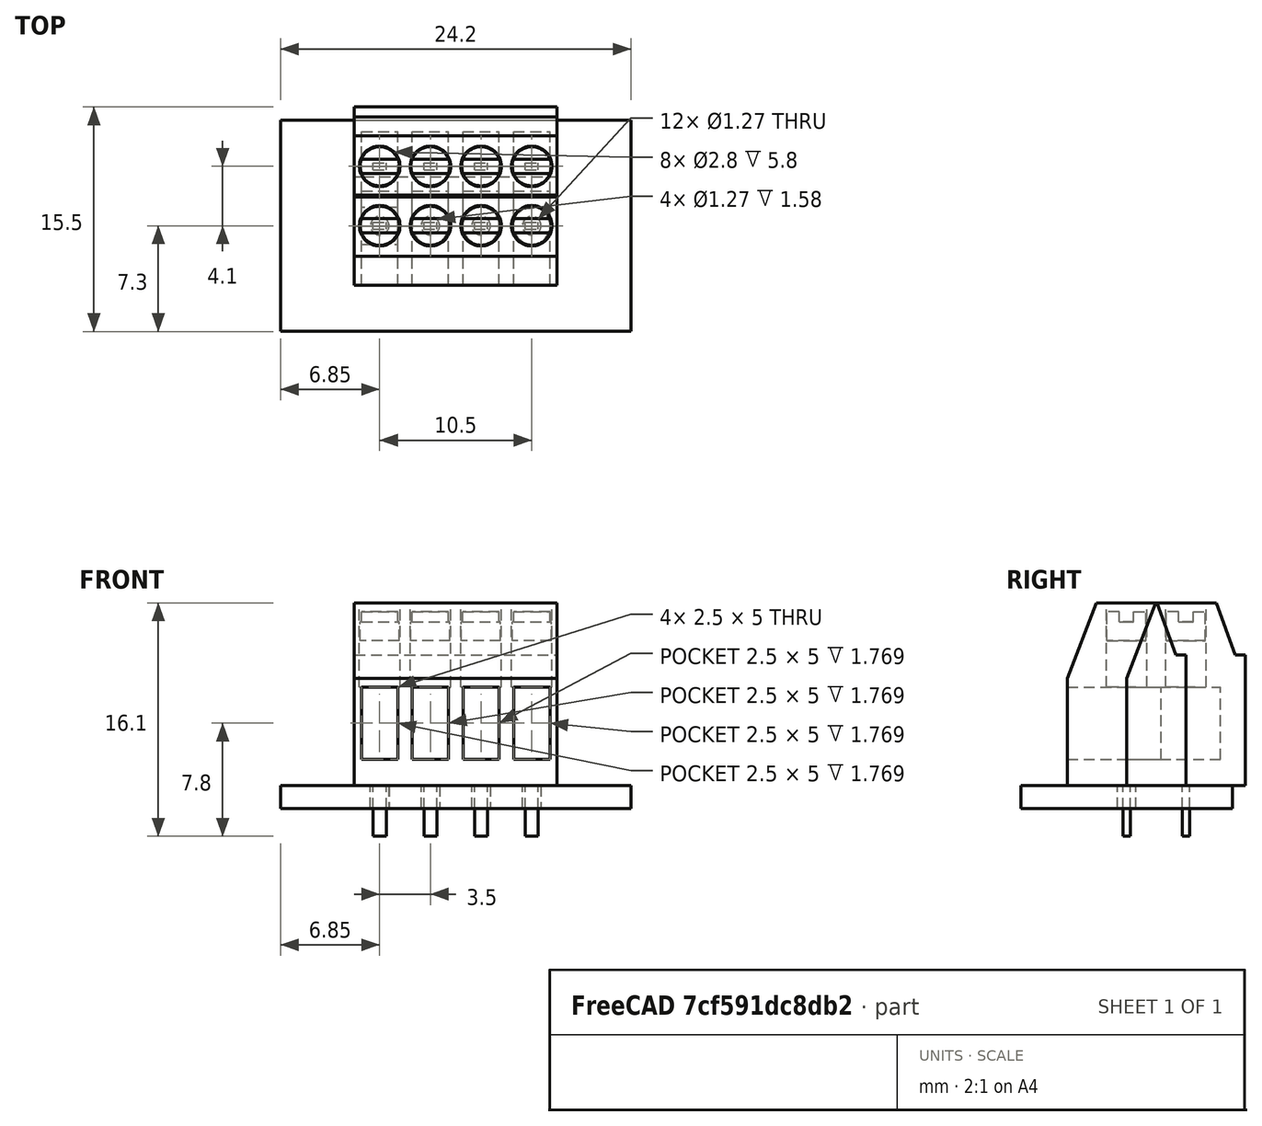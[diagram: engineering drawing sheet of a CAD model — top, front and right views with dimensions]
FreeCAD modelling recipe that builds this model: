
FCSTD DOCUMENT  (FreeCAD 0.18R16131 (Git))
Label: TerminalBlock_TE_284391-4_Angled_1x04_P3.50mm
License: All rights reserved
LicenseURL: http://en.wikipedia.org/wiki/All_rights_reserved
objects: Part::Box×12, Part::Cut×12, Part::Cylinder×8, Part::FeaturePython×6, App::DocumentObjectGroup×2, Part::Part2DObjectPython×1, Part::Extrusion×1, App::Part×1, Part::Feature×1
note: 41 computed .brp shape members not serialized (recipe doc carries the construction recipe); baked Part::Feature solids carry a one-line shape summary decoded from their .brp

FEATURE [Part::Part2DObjectPython] Wire  # Draft 2D object (typed FeaturePython)
  ChamferSize = 0
  Closed = true
  End = (0,0,0)
  FilletRadius = 0
  Length = 38.8989
  MakeFace = true
  Placement = pos=(0,0,0) rot=(0.57735,0.57735,0.57735;2.0944rad)
  Points = (8) [(0,0,0),(0,7.4,0),(2,12.6,0),(6.2,12.6,0),(7.5,9,0),(8.2,9,0),(8.2,0,0),(0,0,0)]
  Start = (0,0,0)
  Subdivisions = 0
FEATURE [Part::Extrusion] Extrude
  Base = -> Wire
  Dir = (1,0,0)
  DirMode = 2
  FaceMakerClass = Part::FaceMakerBullseye
  LengthFwd = 14
  LengthRev = 0
  Solid = false
  Symmetric = true
FEATURE [Part::Box] Box  label="Pin 1"
  AttacherType = Attacher::AttachEngine3D
  Height = 3.5
  Length = 0.9
  Placement = pos=(-5.7,3.85,-3.5) rot=(0,0,1;0rad)
  Width = 0.5
FEATURE [Part::Box] Box001  label="Pin 2"
  AttacherType = Attacher::AttachEngine3D
  Height = 3.5
  Length = 0.9
  Placement = pos=(-2.2,3.85,-3.5) rot=(0,0,1;0rad)
  Width = 0.5
FEATURE [Part::Box] Box002  label="Pin 3"
  AttacherType = Attacher::AttachEngine3D
  Height = 3.5
  Length = 0.9
  Placement = pos=(1.3,3.85,-3.5) rot=(0,0,1;0rad)
  Width = 0.5
FEATURE [Part::Box] Box003  label="Pin 4"
  AttacherType = Attacher::AttachEngine3D
  Height = 3.5
  Length = 0.9
  Placement = pos=(4.8,3.85,-3.5) rot=(0,0,1;0rad)
  Width = 0.5
FEATURE [App::DocumentObjectGroup] Group  label="Pins"
  Group = -> [Box,Box001,Box002,Box003]
FEATURE [Part::Cylinder] Cylinder
  Angle = 360
  AttacherType = Attacher::AttachEngine3D
  Height = 6.1
  Placement = pos=(1.75,4.1,6.8) rot=(0,0,1;0rad)
  Radius = 1.4
FEATURE [Part::Cylinder] Cylinder001
  Angle = 360
  AttacherType = Attacher::AttachEngine3D
  Height = 6.1
  Placement = pos=(5.25,4.1,6.8) rot=(0,0,1;0rad)
  Radius = 1.4
FEATURE [Part::Cylinder] Cylinder002
  Angle = 360
  AttacherType = Attacher::AttachEngine3D
  Height = 6.1
  Placement = pos=(-1.75,4.1,6.8) rot=(0,0,1;0rad)
  Radius = 1.4
FEATURE [Part::Cylinder] Cylinder003
  Angle = 360
  AttacherType = Attacher::AttachEngine3D
  Height = 6.1
  Placement = pos=(-5.25,4.1,6.8) rot=(0,0,1;0rad)
  Radius = 1.4
FEATURE [Part::Cut] Cut
  Base = -> Extrude
  Tool = -> Cylinder
FEATURE [Part::Cut] Cut001
  Base = -> Cut
  Tool = -> Cylinder003
FEATURE [Part::Cut] Cut002
  Base = -> Cut001
  Tool = -> Cylinder002
FEATURE [Part::Cut] Cut003
  Base = -> Cut002
  Tool = -> Cylinder001
FEATURE [Part::Box] Box004  label="Cube"
  AttacherType = Attacher::AttachEngine3D
  Height = 5
  Length = 2.5
  Placement = pos=(-6.5,0,1.8) rot=(0,0,1;0rad)
  Width = 6.5
FEATURE [Part::Box] Box005  label="Cube001"
  AttacherType = Attacher::AttachEngine3D
  Height = 5
  Length = 2.5
  Placement = pos=(-3,0,1.8) rot=(0,0,1;0rad)
  Width = 6.5
FEATURE [Part::Box] Box006  label="Cube002"
  AttacherType = Attacher::AttachEngine3D
  Height = 5
  Length = 2.5
  Placement = pos=(0.5,0,1.8) rot=(0,0,1;0rad)
  Width = 6.5
FEATURE [Part::Box] Box007  label="Cube003"
  AttacherType = Attacher::AttachEngine3D
  Height = 5
  Length = 2.5
  Placement = pos=(4,0,1.8) rot=(0,0,1;0rad)
  Width = 6.5
FEATURE [Part::Cut] Cut004
  Base = -> Cut003
  Tool = -> Box004
FEATURE [Part::Cut] Cut005
  Base = -> Cut004
  Tool = -> Box007
FEATURE [Part::Cut] Cut006
  Base = -> Cut005
  Tool = -> Box006
FEATURE [Part::Cut] Cut007  label="Plastic Body"
  Base = -> Cut006
  Tool = -> Box005
FEATURE [Part::Cylinder] Cylinder004
  Angle = 360
  AttacherType = Attacher::AttachEngine3D
  Height = 2
  Radius = 1.35
FEATURE [Part::Box] Box008  label="Cube004"
  AttacherType = Attacher::AttachEngine3D
  Height = 0.7
  Length = 3
  Placement = pos=(-1.5,-0.5,1.3) rot=(0,0,1;0rad)
  Width = 1
FEATURE [Part::Cut] Cut008  label="Screw 1"
  Base = -> Cylinder004
  Placement = pos=(-5.25,4.1,10) rot=(0,0,1;0rad)
  Tool = -> Box008
FEATURE [Part::Cylinder] Cylinder005
  Angle = 360
  AttacherType = Attacher::AttachEngine3D
  Height = 2
  Radius = 1.35
FEATURE [Part::Box] Box009  label="Cube005"
  AttacherType = Attacher::AttachEngine3D
  Height = 0.7
  Length = 3
  Placement = pos=(-1.5,-0.5,1.3) rot=(0,0,1;0rad)
  Width = 1
FEATURE [Part::Cut] Cut009  label="Screw 2"
  Base = -> Cylinder005
  Placement = pos=(-1.75,4.1,10) rot=(0,0,1;0rad)
  Tool = -> Box009
FEATURE [Part::Cylinder] Cylinder006
  Angle = 360
  AttacherType = Attacher::AttachEngine3D
  Height = 2
  Radius = 1.35
FEATURE [Part::Box] Box010  label="Cube006"
  AttacherType = Attacher::AttachEngine3D
  Height = 0.7
  Length = 3
  Placement = pos=(-1.5,-0.5,1.3) rot=(0,0,1;0rad)
  Width = 1
FEATURE [Part::Cut] Cut010  label="Screw 3"
  Base = -> Cylinder006
  Placement = pos=(1.75,4.1,10) rot=(0,0,1;0rad)
  Tool = -> Box010
FEATURE [Part::Cylinder] Cylinder007
  Angle = 360
  AttacherType = Attacher::AttachEngine3D
  Height = 2
  Radius = 1.35
FEATURE [Part::Box] Box011  label="Cube007"
  AttacherType = Attacher::AttachEngine3D
  Height = 0.7
  Length = 3
  Placement = pos=(-1.5,-0.5,1.3) rot=(0,0,1;0rad)
  Width = 1
FEATURE [Part::Cut] Cut011  label="Screw 4"
  Base = -> Cylinder007
  Placement = pos=(5.25,4.1,10) rot=(0,0,1;0rad)
  Tool = -> Box011
FEATURE [Part::FeaturePython] FFab_lines  label="FFab"  # a2plus imported part (geometry in sourceFile) (typed FeaturePython)
  fixedPosition = true
FEATURE [Part::FeaturePython] Filk_lines  label="FrontSilk"  # a2plus imported part (geometry in sourceFile) (typed FeaturePython)
  fixedPosition = true
FEATURE [Part::FeaturePython] TopPads  # a2plus imported part (geometry in sourceFile) (typed FeaturePython)
  fixedPosition = true
FEATURE [Part::FeaturePython] BotPads  # a2plus imported part (geometry in sourceFile) (typed FeaturePython)
  fixedPosition = true
FEATURE [Part::FeaturePython] THPs  label="PTHs"  # a2plus imported part (geometry in sourceFile) (typed FeaturePython)
  fixedPosition = true
FEATURE [Part::FeaturePython] newPCB  label="Pcb"  # a2plus imported part (geometry in sourceFile) (typed FeaturePython)
  fixedPosition = true
FEATURE [App::DocumentObjectGroup] TerminalBlock_TE_284391_4_Angled_1x04_P3_50mm_fp
  Group = -> [FFab_lines,Filk_lines,TopPads,BotPads,THPs,newPCB]
FEATURE [App::Part] Part  label="TerminalBlock_TE_284391_4_Angled_1x04_P3.5mm"
  Group = -> [Box,Box002,Box003,Box001,Group,Cut002,Cut,Cut004,Cylinder003,Box004,Cylinder002,Extrude,Cylinder001,Cylinder,Wire,Cut005,Cut006,Cut001,Cut003,Box005,Box007,Box006,Cut007,Cylinder004,Box008,Cut008,Cylinder005,Box009,Cut009,Cylinder006,Box010,Cut010,Box011,Cylinder007,Cut011]
  Origin = -> Origin
FEATURE [Part::Feature] Shape001  label="TerminalBlock_TE_284391_4_Angled_1x04_P3_5mm_cp"
  shape: bbox 14 x 8.2 x 16.1 mm, 97 faces, 9 solids (baked)
